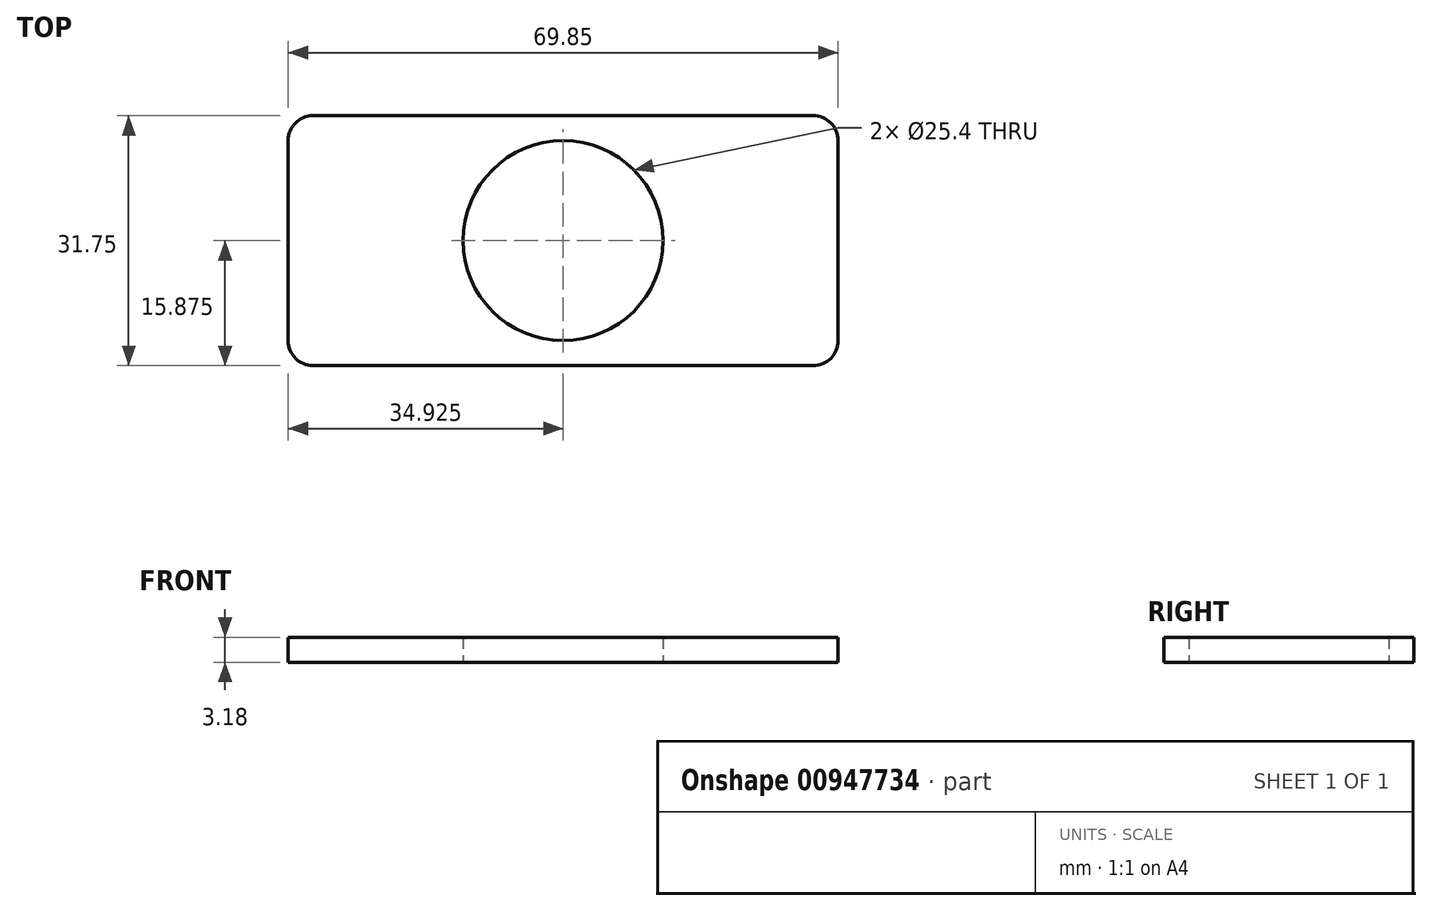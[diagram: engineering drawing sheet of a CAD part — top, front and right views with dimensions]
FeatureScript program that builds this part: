
annotation { "Feature Type Name" : "Feature", "Feature Type Description" : "" }
export const myFeature = defineFeature(function(context is Context, id is Id, definition is map)
    precondition{}
    {
        {
            var Q0;
            Q0=qCreatedBy(makeId("Top.planeOp"),FACE);
            var sketch = newSketch(context, id + "F0", { "sketchPlane" : qUnion([Q0])});
            skLineSegment(sketch, "E0.bottom", {"start": v(-3.18, 0) * mm, "end": v(-66.67, 0) * mm});
            skLineSegment(sketch, "E0.top", {"start": v(-3.18, 31.75) * mm, "end": v(-66.67, 31.75) * mm});
            skLineSegment(sketch, "E0.left", {"start": v(0, 3.17) * mm, "end": v(0, 28.58) * mm});
            skLineSegment(sketch, "E0.right", {"start": v(-69.85, 3.17) * mm, "end": v(-69.85, 28.57) * mm});
            skLineSegment(sketch, "E1", {"start": v(-69.85, 15.88) * mm, "end": v(0, 15.88) * mm, "construction": true});
            skLineSegment(sketch, "E2", {"start": v(-34.92, 31.75) * mm, "end": v(-34.92, 0) * mm, "construction": true});
            skCircle(sketch, "E3", {"center": v(-34.92, 15.88) * mm, "radius": 12.7 * mm});
            skPoint(sketch, "E4.visualSharp", {"position": v(0, 31.75) * mm});
            skArc(sketch, "E4.filletArc", {"start": v(0, 28.58) * mm, "mid": v(-0.93, 30.82) * mm, "end": v(-3.18, 31.75) * mm});
            skPoint(sketch, "E5.visualSharp", {"position": v(0, 0) * mm});
            skArc(sketch, "E5.filletArc", {"start": v(-3.18, 0) * mm, "mid": v(-0.93, 0.93) * mm, "end": v(0, 3.17) * mm});
            skPoint(sketch, "E6.visualSharp", {"position": v(-69.85, 0) * mm});
            skArc(sketch, "E6.filletArc", {"start": v(-69.85, 3.17) * mm, "mid": v(-68.92, 0.93) * mm, "end": v(-66.67, 0) * mm});
            skPoint(sketch, "E7.visualSharp", {"position": v(-69.85, 31.75) * mm});
            skArc(sketch, "E7.filletArc", {"start": v(-66.67, 31.75) * mm, "mid": v(-68.92, 30.82) * mm, "end": v(-69.85, 28.57) * mm});
            skSolve(sketch);
        }
        {
            var Q0;
            Q0=qSketchRegion(id+"F0",true);
            extrude(context, id + "F1", {"entities" : qUnion([Q0]), "depth" : 3.17 * mm});
        }
    });
